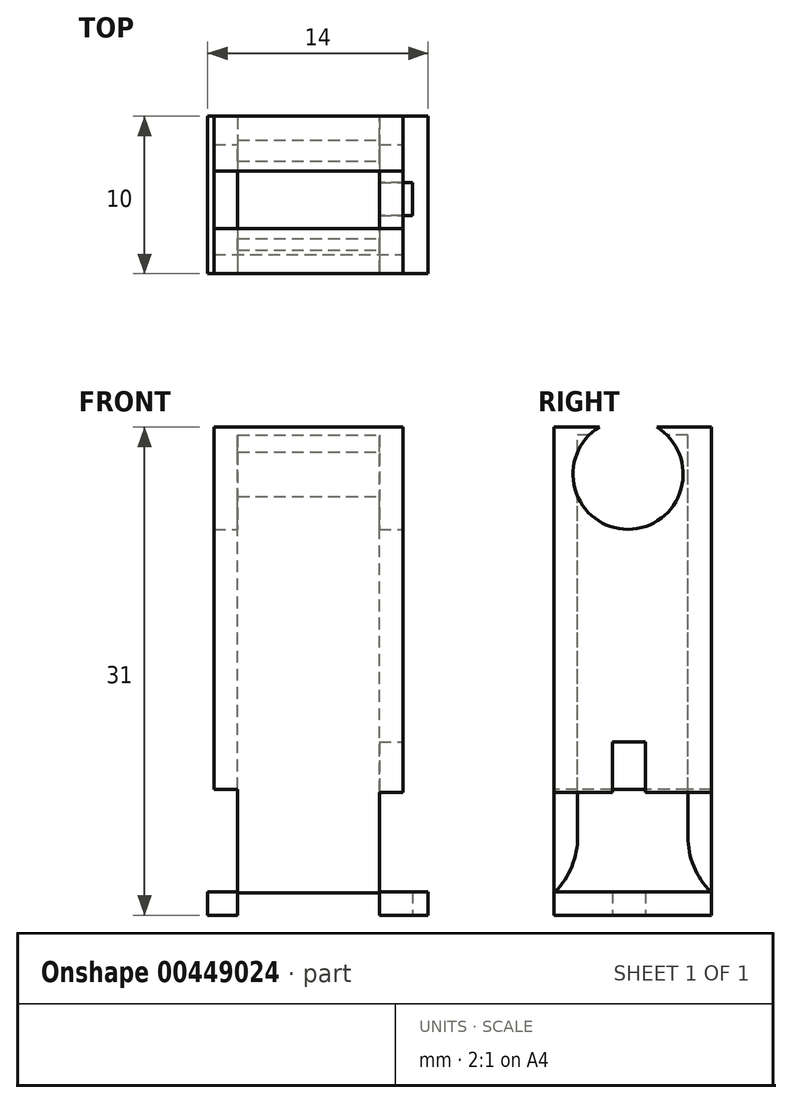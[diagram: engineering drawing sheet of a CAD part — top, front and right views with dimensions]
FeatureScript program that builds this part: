
annotation { "Feature Type Name" : "Feature", "Feature Type Description" : "" }
export const myFeature = defineFeature(function(context is Context, id is Id, definition is map)
    precondition{}
    {
        {
            var Q0;
            Q0=qCreatedBy(makeId("Top.planeOp"),FACE);
            var sketch = newSketch(context, id + "F0", { "sketchPlane" : qUnion([Q0])});
            skLineSegment(sketch, "E0.bottom", {"start": v(0, 0) * mm, "end": v(14, 0) * mm});
            skLineSegment(sketch, "E0.top", {"start": v(0, 10) * mm, "end": v(14, 10) * mm});
            skLineSegment(sketch, "E0.left", {"start": v(0, 0) * mm, "end": v(0, 10) * mm});
            skLineSegment(sketch, "E0.right", {"start": v(14, 0) * mm, "end": v(14, 10) * mm});
            skSolve(sketch);
        }
        {
            var Q0;
            Q0 = qSketchRegion(id + "F0", true);
            extrude(context, id + "F1", {"entities" : qUnion([Q0]), "depth" : 1.5 * mm});
        }
        {
            var Q0;
            Q0=makeQuery(id+"F1.opExtrude","CAP_FACE",FACE,{"disambiguationData":[OSD([sQuery(id+"F0.wireOp",EDGE,"E0.bottom"),sQuery(id+"F0.wireOp",EDGE,"E0.top"),sQuery(id+"F0.wireOp",EDGE,"E0.left"),sQuery(id+"F0.wireOp",EDGE,"E0.right")])],"isStart":false});
            var sketch = newSketch(context, id + "F2", { "sketchPlane" : qUnion([Q0])});
            skLineSegment(sketch, "E1.bottom", {"start": v(1.9, 8.5) * mm, "end": v(10.9, 8.5) * mm});
            skLineSegment(sketch, "E1.top", {"start": v(1.9, 1.5) * mm, "end": v(10.9, 1.5) * mm});
            skLineSegment(sketch, "E1.left", {"start": v(1.9, 8.5) * mm, "end": v(1.9, 1.5) * mm});
            skLineSegment(sketch, "E1.right", {"start": v(10.9, 8.5) * mm, "end": v(10.9, 1.5) * mm});
            skSolve(sketch);
        }
        {
            var Q0;
            Q0 = qSketchRegion(id + "F2", true);
            extrude(context, id + "F3", {"entities" : qUnion([Q0]), "operationType" : NewBodyOperationType.REMOVE, "oppositeDirection" : true, "depth" : 25 * mm});
        }
        {
            var Q0;
            Q0=makeQuery(id+"F1.opExtrude","CAP_FACE",FACE,{"disambiguationData":[OSD([sQuery(id+"F0.wireOp",EDGE,"E0.bottom"),sQuery(id+"F0.wireOp",EDGE,"E0.top"),sQuery(id+"F0.wireOp",EDGE,"E0.left"),sQuery(id+"F0.wireOp",EDGE,"E0.right")])],"isStart":false});
            var sketch = newSketch(context, id + "F4", { "sketchPlane" : qUnion([Q0])});
            skLineSegment(sketch, "E2.bottom", {"start": v(0.4, 10) * mm, "end": v(12.4, 10) * mm});
            skLineSegment(sketch, "E2.top", {"start": v(0.4, 0) * mm, "end": v(12.4, 0) * mm});
            skLineSegment(sketch, "E2.left", {"start": v(0.4, 10) * mm, "end": v(0.4, 0) * mm});
            skLineSegment(sketch, "E2.right", {"start": v(12.4, 10) * mm, "end": v(12.4, 0) * mm});
            skLineSegment(sketch, "E3.bottom", {"start": v(1.9, 8.5) * mm, "end": v(10.9, 8.5) * mm});
            skLineSegment(sketch, "E3.top", {"start": v(1.9, 1.5) * mm, "end": v(10.9, 1.5) * mm});
            skLineSegment(sketch, "E3.left", {"start": v(1.9, 8.5) * mm, "end": v(1.9, 1.5) * mm});
            skLineSegment(sketch, "E3.right", {"start": v(10.9, 8.5) * mm, "end": v(10.9, 1.5) * mm});
            skSolve(sketch);
        }
        {
            var Q0;
            Q0 = qSketchRegion(id + "F4", true);
            extrude(context, id + "F5", {"entities" : qUnion([Q0]), "operationType" : NewBodyOperationType.ADD, "depth" : 29 * mm});
        }
        {
            var Q0;
            Q0=makeQuery(id+"F5.opExtrude","CAP_FACE",FACE,{"disambiguationData":[OSD([sQuery(id+"F4.wireOp",EDGE,"E2.bottom"),sQuery(id+"F4.wireOp",EDGE,"E2.top"),sQuery(id+"F4.wireOp",EDGE,"E2.left"),sQuery(id+"F4.wireOp",EDGE,"E2.right"),sQuery(id+"F4.wireOp",EDGE,"E3.bottom"),sQuery(id+"F4.wireOp",EDGE,"E3.top"),sQuery(id+"F4.wireOp",EDGE,"E3.left"),sQuery(id+"F4.wireOp",EDGE,"E3.right")])],"isStart":false});
            var sketch = newSketch(context, id + "F6", { "sketchPlane" : qUnion([Q0])});
            skLineSegment(sketch, "E4.bottom", {"start": v(12.4, 0) * mm, "end": v(0.4, 0) * mm});
            skLineSegment(sketch, "E4.top", {"start": v(12.4, 10) * mm, "end": v(0.4, 10) * mm});
            skLineSegment(sketch, "E4.left", {"start": v(12.4, 0) * mm, "end": v(12.4, 10) * mm});
            skLineSegment(sketch, "E4.right", {"start": v(0.4, 0) * mm, "end": v(0.4, 10) * mm});
            skSolve(sketch);
        }
        {
            var Q0;
            Q0 = qSketchRegion(id + "F6", true);
            extrude(context, id + "F7", {"entities" : qUnion([Q0]), "operationType" : NewBodyOperationType.ADD, "depth" : 0.5 * mm});
        }
        {
            var Q0;
            Q0=makeQuery(id+"F7.boolean.opBoolean","MERGE",FACE,{"derivedFrom":[makeQuery(id+"F5.opExtrude","SWEPT_FACE",FACE,{"disambiguationData":[OSD([sQuery(id+"F4.wireOp",EDGE,"E2.right")])]}),makeQuery(id+"F7.opExtrude","SWEPT_FACE",FACE,{"disambiguationData":[OSD([sQuery(id+"F6.wireOp",EDGE,"E4.left")])]})]});
            var sketch = newSketch(context, id + "F8", { "sketchPlane" : qUnion([Q0])});
            skCircle(sketch, "E5", {"center": v(4.7, 28.02) * mm, "radius": 3.5 * mm});
            skSolve(sketch);
        }
        {
            var Q0;
            Q0 = qSketchRegion(id + "F8", true);
            extrude(context, id + "F9", {"entities" : qUnion([Q0]), "operationType" : NewBodyOperationType.REMOVE, "oppositeDirection" : true, "depth" : 25 * mm});
        }
        {
            var Q0;
            Q0=makeQuery(id+"F1.opExtrude","CAP_FACE",FACE,{"disambiguationData":[OSD([sQuery(id+"F0.wireOp",EDGE,"E0.bottom"),sQuery(id+"F0.wireOp",EDGE,"E0.top"),sQuery(id+"F0.wireOp",EDGE,"E0.left"),sQuery(id+"F0.wireOp",EDGE,"E0.right")])],"isStart":true});
            var sketch = newSketch(context, id + "F10", { "sketchPlane" : qUnion([Q0])});
            skLineSegment(sketch, "E6.bottom", {"start": v(10.9, -3.7) * mm, "end": v(13, -3.7) * mm});
            skLineSegment(sketch, "E6.top", {"start": v(10.9, -5.8) * mm, "end": v(13, -5.8) * mm});
            skLineSegment(sketch, "E6.left", {"start": v(10.9, -3.7) * mm, "end": v(10.9, -5.8) * mm});
            skLineSegment(sketch, "E6.right", {"start": v(13, -3.7) * mm, "end": v(13, -5.8) * mm});
            skSolve(sketch);
        }
        {
            var Q0;
            Q0 = qSketchRegion(id + "F10", true);
            extrude(context, id + "F11", {"entities" : qUnion([Q0]), "operationType" : NewBodyOperationType.REMOVE, "oppositeDirection" : true, "depth" : 11 * mm});
        }
        {
            var Q0;
            Q0=makeQuery(id+"F7.boolean.opBoolean","MERGE",FACE,{"derivedFrom":[makeQuery(id+"F5.opExtrude","SWEPT_FACE",FACE,{"disambiguationData":[OSD([sQuery(id+"F4.wireOp",EDGE,"E2.left")])]}),makeQuery(id+"F7.opExtrude","SWEPT_FACE",FACE,{"disambiguationData":[OSD([sQuery(id+"F6.wireOp",EDGE,"E4.right")])]})]});
            var sketch = newSketch(context, id + "F12", { "sketchPlane" : qUnion([Q0])});
            skLineSegment(sketch, "E7.bottom", {"start": v(-10, 1.5) * mm, "end": v(0, 1.5) * mm});
            skLineSegment(sketch, "E7.top", {"start": v(-10, 8) * mm, "end": v(0, 8) * mm});
            skLineSegment(sketch, "E7.left", {"start": v(-10, 1.5) * mm, "end": v(-10, 8) * mm});
            skLineSegment(sketch, "E7.right", {"start": v(0, 1.5) * mm, "end": v(0, 8) * mm});
            skSolve(sketch);
        }
        {
            var Q0;
            Q0 = qSketchRegion(id + "F12", true);
            extrude(context, id + "F13", {"entities" : qUnion([Q0]), "operationType" : NewBodyOperationType.REMOVE, "oppositeDirection" : true, "depth" : 1.5 * mm});
        }
        {
            var Q0;
            Q0=makeQuery(id+"F7.boolean.opBoolean","MERGE",FACE,{"derivedFrom":[makeQuery(id+"F5.opExtrude","SWEPT_FACE",FACE,{"disambiguationData":[OSD([sQuery(id+"F4.wireOp",EDGE,"E2.right")])]}),makeQuery(id+"F7.opExtrude","SWEPT_FACE",FACE,{"disambiguationData":[OSD([sQuery(id+"F6.wireOp",EDGE,"E4.left")])]})]});
            var sketch = newSketch(context, id + "F14", { "sketchPlane" : qUnion([Q0])});
            skLineSegment(sketch, "E8.bottom", {"start": v(0, 1.5) * mm, "end": v(10, 1.5) * mm});
            skLineSegment(sketch, "E8.top", {"start": v(0, 7.8) * mm, "end": v(10, 7.8) * mm});
            skLineSegment(sketch, "E8.left", {"start": v(0, 1.5) * mm, "end": v(0, 7.8) * mm});
            skLineSegment(sketch, "E8.right", {"start": v(10, 1.5) * mm, "end": v(10, 7.8) * mm});
            skSolve(sketch);
        }
        {
            var Q0;
            Q0 = qSketchRegion(id + "F14", true);
            extrude(context, id + "F15", {"entities" : qUnion([Q0]), "operationType" : NewBodyOperationType.REMOVE, "oppositeDirection" : true, "depth" : 1.5 * mm});
        }
        {
            var Q0;
            Q0=makeQuery(id+"F3.boolean.opBoolean","INTERSECT",EDGE,{"derivedFrom":[makeQuery(id+"F1.opExtrude","CAP_FACE",FACE,{"disambiguationData":[OSD([sQuery(id+"F0.wireOp",EDGE,"E0.bottom"),sQuery(id+"F0.wireOp",EDGE,"E0.top"),sQuery(id+"F0.wireOp",EDGE,"E0.left"),sQuery(id+"F0.wireOp",EDGE,"E0.right")])],"isStart":true}),makeQuery(id+"F3.opExtrude","SWEPT_FACE",FACE,{"disambiguationData":[OSD([sQuery(id+"F2.wireOp",EDGE,"E1.bottom")])]})]});
            var Q1;
            Q1=makeQuery(id+"F3.boolean.opBoolean","INTERSECT",EDGE,{"derivedFrom":[makeQuery(id+"F1.opExtrude","CAP_FACE",FACE,{"disambiguationData":[OSD([sQuery(id+"F0.wireOp",EDGE,"E0.bottom"),sQuery(id+"F0.wireOp",EDGE,"E0.top"),sQuery(id+"F0.wireOp",EDGE,"E0.left"),sQuery(id+"F0.wireOp",EDGE,"E0.right")])],"isStart":true}),makeQuery(id+"F3.opExtrude","SWEPT_FACE",FACE,{"disambiguationData":[OSD([sQuery(id+"F2.wireOp",EDGE,"E1.top")])]})]});
            fillet(context, id + "F16", {"entities" : qUnion([Q0, Q1]), "radius" : 5 * mm, "tangentPropagation" : true, "allowEdgeOverflow" : false});
        }
    });
